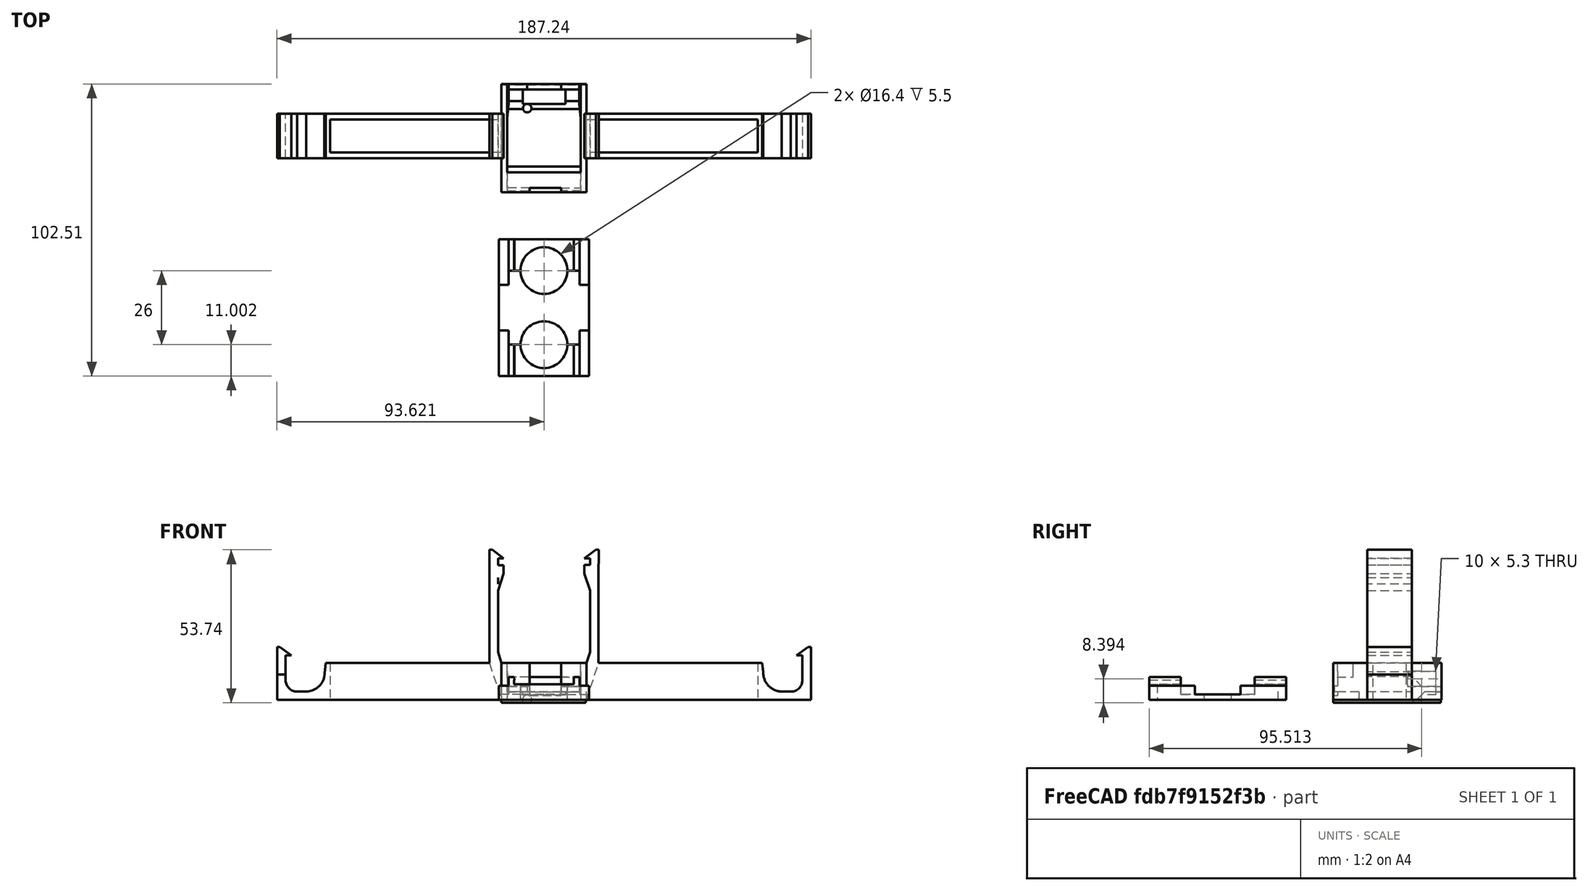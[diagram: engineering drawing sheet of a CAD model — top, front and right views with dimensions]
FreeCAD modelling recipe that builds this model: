
FCSTD DOCUMENT  (FreeCAD 0.18.4R)
Label: hanger.sonic.sensor
License: All rights reserved
LicenseURL: http://en.wikipedia.org/wiki/All_rights_reserved
objects: Part::Part2DObjectPython×4, Part::Feature×3, Part::Extrusion×3, Part::Cut×2
note: 12 computed .brp shape members not serialized (recipe doc carries the construction recipe); baked Part::Feature solids carry a one-line shape summary decoded from their .brp

FEATURE [Part::Feature] Fusion009012003002002002002004002005003  label="Fusion009012003002002002002004002005004"
  Placement = pos=(-7.01207e-05,-307.815,-201.044) rot=(1,0,0;3.14159rad)
  shape: bbox 31.67 x 48 x 8 mm, 52 faces (baked)
FEATURE [Part::Feature] Fusion009012003002002002002004002005004  label="Fusion009012003002002002002004002005005"
  shape: bbox 187.2 x 38 x 52.74 mm, 129 faces, 2 solids (baked)
FEATURE [Part::Part2DObjectPython] Line  # Draft 2D object (typed FeaturePython)
  ChamferSize = 0
  Closed = false
  End = (71.2576,-114.027,-125.386)
  FilletRadius = 0
  Length = 3
  MakeFace = true
  Placement = pos=(68.2576,-114.027,-125.386) rot=(0,0,1;0rad)
  Points = (2) [(0,0,0),(3,0,-5.68434e-14)]
  Start = (68.2576,-114.027,-125.386)
  Subdivisions = 0
  Support = -> [Fusion009012003002002002002004002005004]
FEATURE [Part::Feature] Face
  shape: bbox 2.02e-05 x 3.643 x 0.921 mm, 1 faces, 0 solids (baked)
FEATURE [Part::Extrusion] Extrusion
  Base = -> Face
  Dir = (-10,-3e-16,4e-15)
  DirMode = 0
  FaceMakerClass = Part::FaceMakerBullseye
  LengthFwd = 0
  LengthRev = 0
  Solid = true
  Symmetric = false
FEATURE [Part::Cut] Cut
  Base = -> Fusion009012003002002002002004002005004
  Tool = -> Extrusion
FEATURE [Part::Part2DObjectPython] Rectangle  # Draft 2D object (typed FeaturePython)
  ChamferSize = 0
  Columns = 1
  FilletRadius = 0
  Height = 37.7082
  Length = 29.5561
  MakeFace = true
  Placement = pos=(60.7576,-105.819,-125.386) rot=(1,0,0;3.14159rad)
  Rows = 1
  Support = -> [Cut]
FEATURE [Part::Part2DObjectPython] Line001  # Draft 2D object (typed FeaturePython)
  ChamferSize = 0
  Closed = false
  End = (90.5576,-143.527,-126.386)
  FilletRadius = 0
  Length = 1
  MakeFace = true
  Placement = pos=(90.5576,-143.527,-125.386) rot=(0.57735,0.57735,0.57735;2.0944rad)
  Points = (2) [(0,0,0),(0,-1,0)]
  Start = (90.5576,-143.527,-125.386)
  Subdivisions = 0
  Support = -> [Cut]
FEATURE [Part::Extrusion] Extrusion001
  Base = -> Rectangle
  Dir = (-2.8e-15,-1.09e-14,-1)
  DirMode = 0
  FaceMakerClass = Part::FaceMakerBullseye
  LengthFwd = 0
  LengthRev = 0
  Solid = true
  Symmetric = false
FEATURE [Part::Part2DObjectPython] Circle  # Draft 2D object (typed FeaturePython)
  FirstAngle = 0
  LastAngle = 0
  MakeFace = true
  Placement = pos=(69.7576,-114.027,-125.386) rot=(0,0,-1;1.5708rad)
  Radius = 1.5
  Support = -> [Extrusion001]
FEATURE [Part::Extrusion] Extrusion002
  Base = -> Circle
  Dir = (-1.453e-13,-5.611e-13,-51.2818)
  DirMode = 0
  FaceMakerClass = Part::FaceMakerBullseye
  LengthFwd = 0
  LengthRev = 0
  Solid = true
  Symmetric = false
FEATURE [Part::Cut] Cut001
  Base = -> Extrusion001
  Tool = -> Extrusion002
